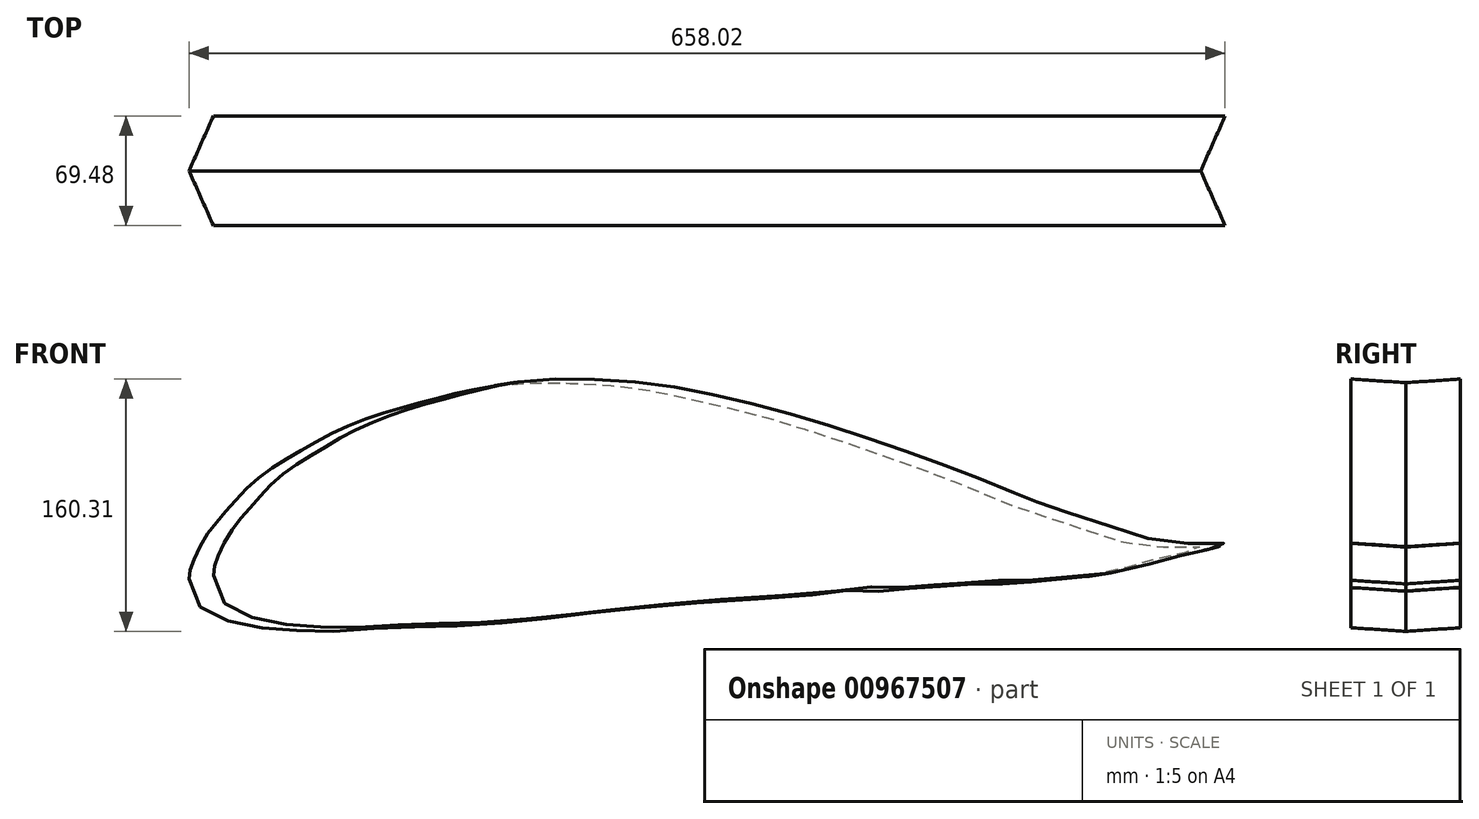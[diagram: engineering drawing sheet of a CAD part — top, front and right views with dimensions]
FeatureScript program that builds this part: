
annotation { "Feature Type Name" : "Feature", "Feature Type Description" : "" }
export const myFeature = defineFeature(function(context is Context, id is Id, definition is map)
    precondition{}
    {
        {
            var Q0;
            Q0=qCreatedBy(makeId("Front.planeOp"),FACE);
            var sketch = newSketch(context, id + "F0", { "sketchPlane" : qUnion([Q0])});
            skFitSpline(sketch, "E0", {"points": [v(4.05, 45.31) * mm, v(5.78, 54.54) * mm, v(15, 73) * mm, v(28.27, 89.14) * mm, v(45.57, 107.6) * mm, v(69.8, 123.74) * mm, v(96.32, 138.73) * mm, v(129.76, 151.42) * mm, v(163.21, 160.64) * mm, v(201.85, 168.72) * mm, v(240.48, 169.87) * mm, v(284.3, 166.99) * mm, v(323.52, 159.5) * mm, v(366.2, 149.11) * mm, v(407.72, 136.42) * mm, v(448.08, 122.58) * mm, v(486.14, 108.75) * mm, v(519.67, 94.87) * mm, v(531.8, 90.25) * mm, v(577.47, 75.22) * mm, v(615.05, 65.97) * mm, v(646.55, 65.4) * mm, v(633.55, 61.34) * mm, v(611, 56.14) * mm, v(577.47, 47.47) * mm, v(527.76, 42.85) * mm, v(519.67, 42.27) * mm, v(503.48, 42.27) * mm, v(481.52, 40.54) * mm, v(463.02, 39.38) * mm, v(444.52, 37.64) * mm, v(424.87, 38.22) * mm, v(404.64, 35.91) * mm, v(343.94, 31.29) * mm, v(280.36, 26.08) * mm, v(239.9, 21.46) * mm, v(201.16, 17.41) * mm, v(162.43, 15.1) * mm, v(130.06, 14.52) * mm, v(97.7, 12.21) * mm, v(71.08, 12.8) * mm, v(48.06, 14.52) * mm, v(25.62, 19.7) * mm, v(10.08, 28.9) * mm, v(4.05, 45.31) * mm]});
            skSolve(sketch);
        }
        {
            var Q0;
            Q0=qCreatedBy(makeId("Top.planeOp"),FACE);
            var sketch = newSketch(context, id + "F1", { "sketchPlane" : qUnion([Q0])});
            skLineSegment(sketch, "E1", {"start": v(4.05, -110.52) * mm, "end": v(4.05, 165.75) * mm, "construction": true});
            skPoint(sketch, "E2", {"position": v(4.05, 0) * mm});
            skLineSegment(sketch, "E3", {"start": v(4.05, 0) * mm, "end": v(18.19, 31.75) * mm});
            skLineSegment(sketch, "E4", {"start": v(4.05, 0) * mm, "end": v(134.8, 0) * mm, "construction": true});
            skLineSegment(sketch, "E5", {"start": v(18.19, 0) * mm, "end": v(18.19, 31.75) * mm, "construction": true});
            skSolve(sketch);
        }
        {
            var Q0;
            Q0=sQuery(id+"F1.wireOp",EDGE,"E3");
            var Q1;
            Q1=sQuery(id+"F1.wireOp",EDGE,"E1");
            cPlane(context, id + "F2", {"entities" : qUnion([Q0, Q1]), "cplaneType" : CPlaneType.LINE_ANGLE, "offset" : 25.4 * mm, "angle" : 90 * degree, "width" : 152.4 * mm, "height" : 152.4 * mm});
        }
        {
            var Q0;
            Q0=qCreatedBy(id+"F2.planeOp",FACE);
            var sketch = newSketch(context, id + "F3", { "sketchPlane" : qUnion([Q0])});
            skLineSegment(sketch, "E6.0", {"start": v(1.65, 0) * mm, "end": v(36.4, 0) * mm, "construction": true});
            skLineSegment(sketch, "E7", {"start": v(1.65, 0) * mm, "end": v(39.68, 2.33) * mm});
            skSolve(sketch);
        }
        {
            var Q0;
            Q0 = qSketchRegion(id + "F0", true);
            var Q1;
            Q1 = qConstructionFilter(qBodyType(qCreatedBy(id + "F3" ,EDGE), BodyType.WIRE), ConstructionObject.NO);
            sweep(context, id + "F4", {"profiles" : qUnion([Q0]), "path" : qUnion([Q1])});
        }
        {
            var Q0;
            Q0=makeQuery(id+"F4.opSweep","SWEPT_BODY",BODY,{"disambiguationData":[OSD([sQuery(id+"F0.wireOp",EDGE,"E0"),sQuery(id+"F3.wireOp",EDGE,"l7S8t43I-mMNO-KOTq-Vje2-cWVaEwsp7xa0")])]});
            var Q1;
            Q1=qCreatedBy(makeId("Front.planeOp"),FACE);
            mirror(context, id + "F5", {"entities" : qUnion([Q0]), "mirrorPlane" : qUnion([Q1])});
        }
    });
